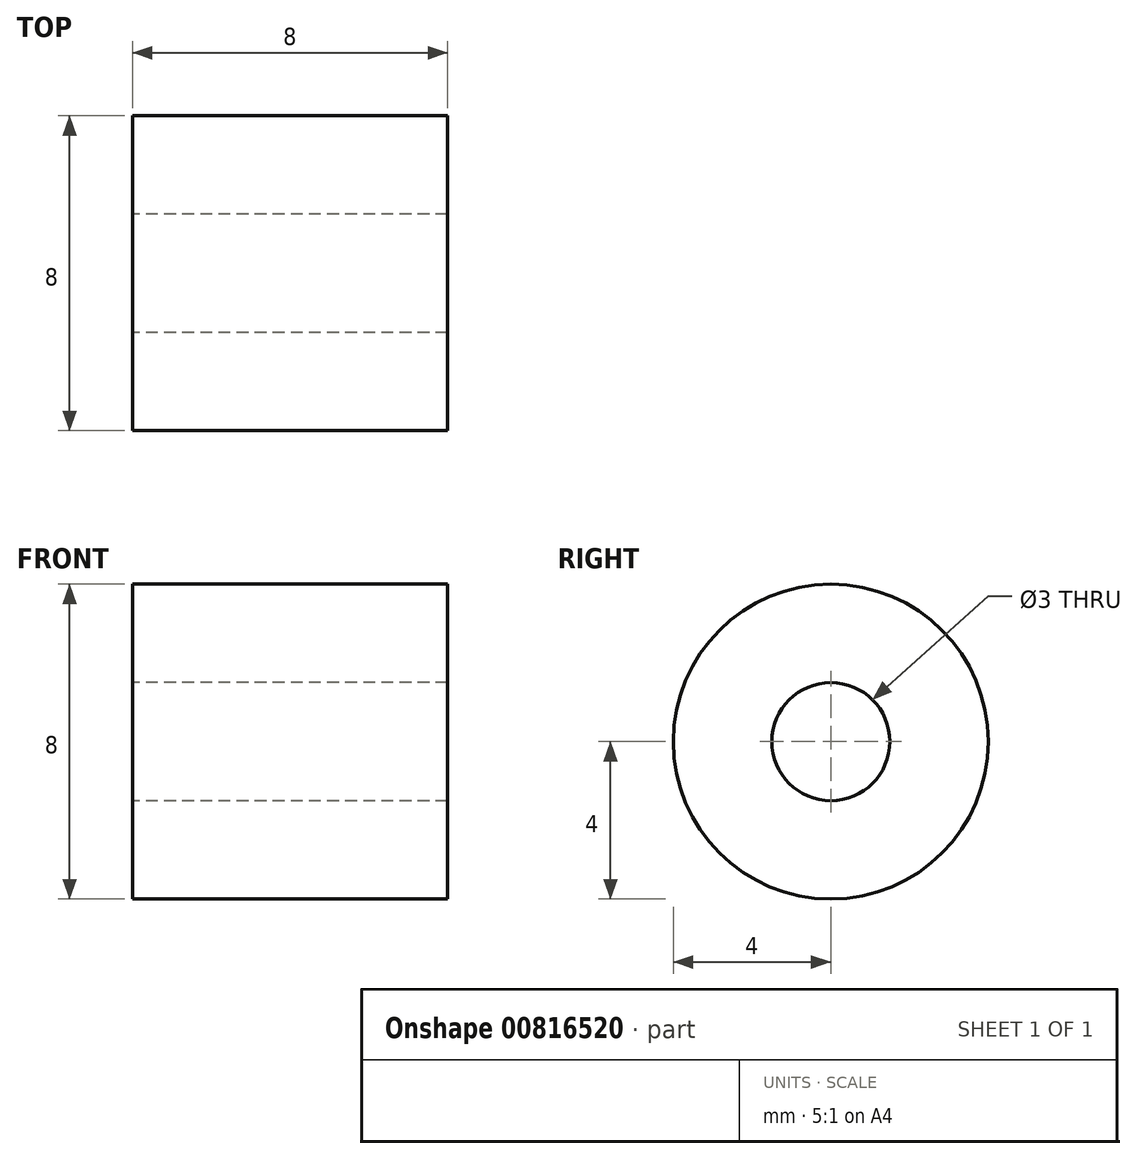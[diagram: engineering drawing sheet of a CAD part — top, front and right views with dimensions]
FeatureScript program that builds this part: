
annotation { "Feature Type Name" : "Feature", "Feature Type Description" : "" }
export const myFeature = defineFeature(function(context is Context, id is Id, definition is map)
    precondition{}
    {
        {
            var Q0;
            Q0=qCreatedBy(makeId("Right.planeOp"),FACE);
            var sketch = newSketch(context, id + "F0", { "sketchPlane" : qUnion([Q0])});
            skCircle(sketch, "E0", {"center": v(0, 0) * mm, "radius": 1.5 * mm});
            skCircle(sketch, "E1", {"center": v(0, 0) * mm, "radius": 4 * mm});
            skSolve(sketch);
        }
        {
            var Q0;
            Q0 = qSketchRegion(id + "F0", true);
            extrude(context, id + "F1", {"entities" : qUnion([Q0]), "depth" : 8 * mm, "offsetDistance" : 25 * mm});
        }
    });
